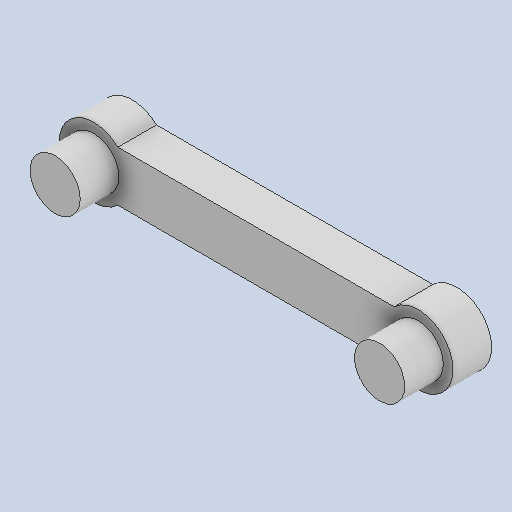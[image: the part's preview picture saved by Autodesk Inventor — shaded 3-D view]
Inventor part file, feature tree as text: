
AUTODESK INVENTOR PART (.ipt)
format: ipt  version: 2022 (Build 260153000, 153)  size: 116,736 bytes
history: native  units: in
note: dims shown in document units (in); Inventor stores cm internally (conversion verified against a paired STEP export)
features: other x3, sketch x1
ambient origin geometry x8: Origin, YZ Plane, XZ Plane, XY Plane, X Axis, Y Axis, Z Axis, Center Point
bodies: Solid1 (feature_tree)
feature tree (4):
  other  "Component25.ipt"
  other  "Solid2::Component25.ipt"
  other  "TaggingFeature1"
  sketch  "Sketch2"  dims[d0=0.3937in]
